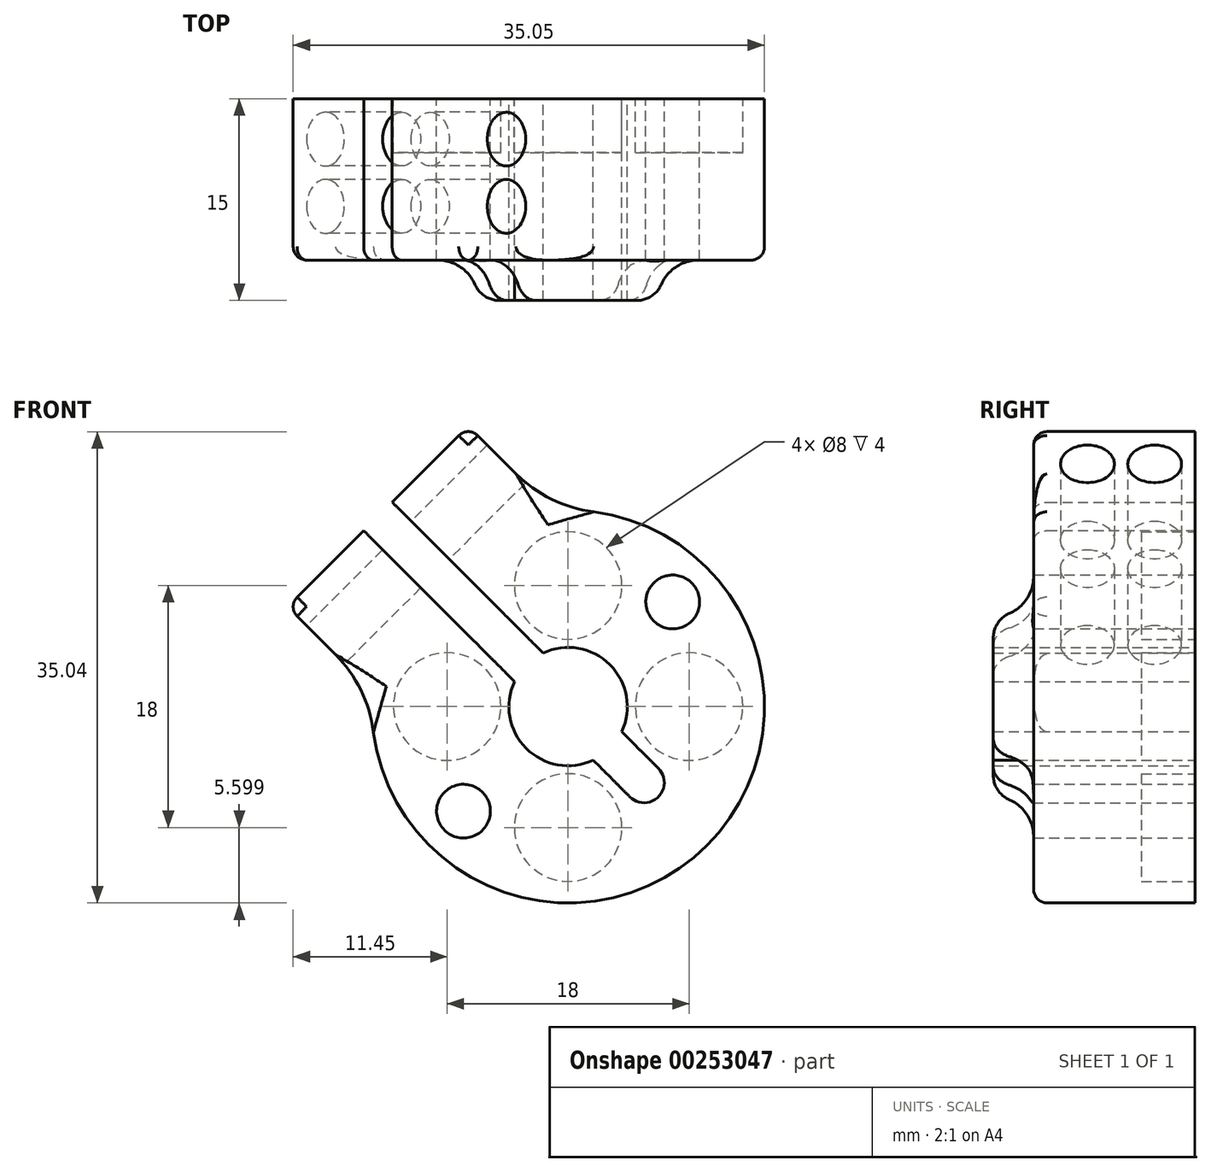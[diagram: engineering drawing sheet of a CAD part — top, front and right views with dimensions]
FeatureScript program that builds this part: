
annotation { "Feature Type Name" : "Feature", "Feature Type Description" : "" }
export const myFeature = defineFeature(function(context is Context, id is Id, definition is map)
    precondition{}
    {
        {
            var Q0;
            Q0=qCreatedBy(makeId("Right.planeOp"),FACE);
            var sketch = newSketch(context, id + "F0", { "sketchPlane" : qUnion([Q0])});
            skLineSegment(sketch, "E0", {"start": v(-60.78, -4.86) * mm, "end": v(-45.78, -4.86) * mm});
            skLineSegment(sketch, "E1", {"start": v(-45.78, -4.86) * mm, "end": v(-45.78, 5.34) * mm});
            skLineSegment(sketch, "E2", {"start": v(-45.78, 5.34) * mm, "end": v(-57.78, 5.34) * mm});
            skLineSegment(sketch, "E3", {"start": v(-57.78, 5.34) * mm, "end": v(-57.78, -2.16) * mm});
            skLineSegment(sketch, "E4", {"start": v(-57.78, -2.16) * mm, "end": v(-60.78, -2.16) * mm});
            skLineSegment(sketch, "E5", {"start": v(-60.78, -2.16) * mm, "end": v(-60.78, -4.86) * mm});
            skLineSegment(sketch, "E6", {"start": v(-43.04, -9.26) * mm, "end": v(-64.3, -9.26) * mm, "construction": true});
            skSolve(sketch);
        }
        {
            var Q0;
            Q0=qSketchRegion(id+"F0",true);
            var Q1;
            Q1=sQuery(id+"F0.wireOp",EDGE,"E6");
            revolve(context, id + "F1", {"entities" : qUnion([Q0]), "axis" : qUnion([Q1]), "revolveType" : RevolveType.FULL});
        }
        {
            var Q0;
            Q0=makeQuery(id+"F1.opRevolve","SWEPT_EDGE",EDGE,{"disambiguationData":[OSD([sQuery(id+"F0.wireOp",EDGE,"E4"),sQuery(id+"F0.wireOp",EDGE,"E5")])]});
            fillet(context, id + "F2", {"entities" : qUnion([Q0]), "radius" : 2 * mm, "tangentPropagation" : true, "allowEdgeOverflow" : false});
        }
        {
            var Q0;
            Q0=makeQuery(id+"F1.opRevolve","SWEPT_FACE",FACE,{"disambiguationData":[OSD([sQuery(id+"F0.wireOp",EDGE,"E1")])]});
            var sketch = newSketch(context, id + "F3", { "sketchPlane" : qUnion([Q0])});
            skCircle(sketch, "E7", {"center": v(0, -0.26) * mm, "radius": 4 * mm});
            skPoint(sketch, "E8", {"position": v(0, -9.26) * mm});
            skCircle(sketch, "E9.1.0", {"center": v(-9, -9.26) * mm, "radius": 4 * mm});
            skCircle(sketch, "E9.2.0", {"center": v(0, -18.26) * mm, "radius": 4 * mm});
            skCircle(sketch, "E9.3.0", {"center": v(9, -9.26) * mm, "radius": 4 * mm});
            skSolve(sketch);
        }
        {
            var Q0;
            Q0=makeQuery(id+"F3.imprint","IMPRINT",FACE,{"disambiguationData":[TD([[makeQuery(id+"F3.imprint","IMPRINT",EDGE,{"derivedFrom":sQuery(id+"F3.wireOp",EDGE,"E7")}),1.0]])]});
            var Q1;
            Q1=makeQuery(id+"F3.imprint","IMPRINT",FACE,{"disambiguationData":[TD([[makeQuery(id+"F3.imprint","IMPRINT",EDGE,{"derivedFrom":sQuery(id+"F3.wireOp",EDGE,"E9.1.0")}),1.0]])]});
            var Q2;
            Q2=makeQuery(id+"F3.imprint","IMPRINT",FACE,{"disambiguationData":[TD([[makeQuery(id+"F3.imprint","IMPRINT",EDGE,{"derivedFrom":sQuery(id+"F3.wireOp",EDGE,"E9.2.0")}),1.0]])]});
            var Q3;
            Q3=makeQuery(id+"F3.imprint","IMPRINT",FACE,{"disambiguationData":[TD([[makeQuery(id+"F3.imprint","IMPRINT",EDGE,{"derivedFrom":sQuery(id+"F3.wireOp",EDGE,"E9.3.0")}),1.0]])]});
            extrude(context, id + "F4", {"entities" : qUnion([Q0, Q1, Q2, Q3]), "operationType" : NewBodyOperationType.REMOVE, "oppositeDirection" : true, "depth" : 4 * mm});
        }
        {
            var Q0;
            Q0=makeQuery(id+"F1.opRevolve","SWEPT_FACE",FACE,{"disambiguationData":[OSD([sQuery(id+"F0.wireOp",EDGE,"E1")])]});
            var sketch = newSketch(context, id + "F5", { "sketchPlane" : qUnion([Q0])});
            skLineSegment(sketch, "E10.0", {"start": v(1.96, -9.42) * mm, "end": v(14.69, 3.3) * mm});
            skLineSegment(sketch, "E11.0", {"start": v(-0.16, -7.3) * mm, "end": v(12.57, 5.43) * mm});
            skLineSegment(sketch, "E12", {"start": v(12.57, 5.43) * mm, "end": v(14.69, 3.3) * mm});
            skLineSegment(sketch, "E13", {"start": v(-0.16, -7.3) * mm, "end": v(1.96, -9.42) * mm});
            skLineSegment(sketch, "E14", {"start": v(0, -9.26) * mm, "end": v(15.38, 6.12) * mm, "construction": true});
            skSolve(sketch);
        }
        {
            var Q0;
            Q0=qSketchRegion(id+"F5",true);
            extrude(context, id + "F6", {"entities" : qUnion([Q0]), "operationType" : NewBodyOperationType.REMOVE, "oppositeDirection" : true, "depth" : 25 * mm});
        }
        {
            var Q0;
            Q0=makeQuery(id+"F1.opRevolve","SWEPT_FACE",FACE,{"disambiguationData":[OSD([sQuery(id+"F0.wireOp",EDGE,"E1")])]});
            var sketch = newSketch(context, id + "F7", { "sketchPlane" : qUnion([Q0])});
            skPoint(sketch, "E15", {"position": v(0, -9.26) * mm});
            skLineSegment(sketch, "E16", {"start": v(7.14, 0) * mm, "end": v(13.08, 5.94) * mm});
            skPoint(sketch, "E16.startSnap0", {"position": v(7.66, -3.72) * mm});
            skLineSegment(sketch, "E17", {"start": v(13.08, 5.94) * mm, "end": v(7.42, 11.6) * mm});
            skLineSegment(sketch, "E18", {"start": v(7.42, 11.6) * mm, "end": v(1.12, 5.3) * mm});
            skLineSegment(sketch, "E19", {"start": v(1.12, 5.3) * mm, "end": v(7.14, 0) * mm});
            skLineSegment(sketch, "E20", {"start": v(0, -9.26) * mm, "end": v(12.98, 3.71) * mm, "construction": true});
            skLineSegment(sketch, "E21.MirrorCS", {"start": v(15.2, 3.82) * mm, "end": v(20.86, -1.84) * mm});
            skLineSegment(sketch, "E22.MirrorCS", {"start": v(20.86, -1.84) * mm, "end": v(14.56, -8.14) * mm});
            skLineSegment(sketch, "E23.MirrorCS", {"start": v(14.56, -8.14) * mm, "end": v(9.26, -2.12) * mm});
            skLineSegment(sketch, "E24.MirrorCS", {"start": v(9.26, -2.12) * mm, "end": v(15.2, 3.82) * mm});
            skSolve(sketch);
        }
        {
            var Q0;
            Q0=qSketchRegion(id+"F7",true);
            var Q1;
            Q1=makeQuery(id+"F1.opRevolve","SWEPT_FACE",FACE,{"disambiguationData":[OSD([sQuery(id+"F0.wireOp",EDGE,"E3")])]});
            extrude(context, id + "F8", {"entities" : qUnion([Q0]), "operationType" : NewBodyOperationType.ADD, "endBound" : BoundingType.UP_TO_SURFACE, "oppositeDirection" : true, "endBoundEntityFace" : qUnion([Q1]), "depth" : 25 * mm});
        }
        {
            var Q0;
            Q0=makeQuery(id+"F1.opRevolve","SWEPT_EDGE",EDGE,{"disambiguationData":[OSD([sQuery(id+"F0.wireOp",EDGE,"E3"),sQuery(id+"F0.wireOp",EDGE,"E4")])]});
            fillet(context, id + "F9", {"entities" : qUnion([Q0]), "radius" : 3 * mm, "tangentPropagation" : true, "allowEdgeOverflow" : false});
        }
        {
            var Q0;
            Q0=makeQuery(id+"F1.opRevolve","SWEPT_EDGE",EDGE,{"disambiguationData":[OSD([sQuery(id+"F0.wireOp",EDGE,"E2"),sQuery(id+"F0.wireOp",EDGE,"E3")])]});
            var Q1;
            Q1=makeQuery(id+"F8.opExtrude","CAP_EDGE",EDGE,{"disambiguationData":[OSD([sQuery(id+"F7.wireOp",EDGE,"E18")])],"isStart":false});
            var Q2;
            Q2=makeQuery(id+"F8.opExtrude","CAP_EDGE",EDGE,{"disambiguationData":[OSD([sQuery(id+"F7.wireOp",EDGE,"E17")])],"isStart":false});
            var Q3;
            Q3=makeQuery(id+"F8.opExtrude","CAP_EDGE",EDGE,{"disambiguationData":[OSD([sQuery(id+"F7.wireOp",EDGE,"E21.MirrorCS")])],"isStart":false});
            var Q4;
            Q4=makeQuery(id+"F8.opExtrude","CAP_EDGE",EDGE,{"disambiguationData":[OSD([sQuery(id+"F7.wireOp",EDGE,"E22.MirrorCS")])],"isStart":false});
            fillet(context, id + "F10", {"entities" : qUnion([Q0, Q1, Q2, Q3, Q4]), "radius" : 1 * mm, "tangentPropagation" : true, "allowEdgeOverflow" : false});
        }
        {
            var Q0;
            Q0=makeQuery(id+"F8.boolean.opBoolean","INTERSECT",EDGE,{"derivedFrom":[makeQuery(id+"F1.opRevolve","SWEPT_FACE",FACE,{"disambiguationData":[OSD([sQuery(id+"F0.wireOp",EDGE,"E2")])]}),makeQuery(id+"F8.opExtrude","SWEPT_FACE",FACE,{"disambiguationData":[OSD([sQuery(id+"F7.wireOp",EDGE,"E18")])]})]});
            var Q1;
            Q1=makeQuery(id+"F8.boolean.opBoolean","INTERSECT",EDGE,{"derivedFrom":[makeQuery(id+"F1.opRevolve","SWEPT_FACE",FACE,{"disambiguationData":[OSD([sQuery(id+"F0.wireOp",EDGE,"E2")])]}),makeQuery(id+"F8.opExtrude","SWEPT_FACE",FACE,{"disambiguationData":[OSD([sQuery(id+"F7.wireOp",EDGE,"E22.MirrorCS")])]})]});
            var Q2;
            Q2=makeQuery(id+"F10.opFillet","BLEND_EDGE",EDGE,{"blendedFrom":[makeQuery(id+"F8.opExtrude","CAP_EDGE",EDGE,{"disambiguationData":[OSD([sQuery(id+"F7.wireOp",EDGE,"E18")])],"isStart":false}),makeQuery(id+"F1.opRevolve","SWEPT_EDGE",EDGE,{"disambiguationData":[OSD([sQuery(id+"F0.wireOp",EDGE,"E2"),sQuery(id+"F0.wireOp",EDGE,"E3")])]})],"blendedInto":[]});
            var Q3;
            Q3=makeQuery(id+"F10.opFillet","BLEND_EDGE",EDGE,{"blendedFrom":[makeQuery(id+"F8.opExtrude","CAP_EDGE",EDGE,{"disambiguationData":[OSD([sQuery(id+"F7.wireOp",EDGE,"E22.MirrorCS")])],"isStart":false}),makeQuery(id+"F1.opRevolve","SWEPT_EDGE",EDGE,{"disambiguationData":[OSD([sQuery(id+"F0.wireOp",EDGE,"E2"),sQuery(id+"F0.wireOp",EDGE,"E3")])]})],"blendedInto":[]});
            fillet(context, id + "F11", {"entities" : qUnion([Q0, Q1, Q2, Q3]), "radius" : 10 * mm, "tangentPropagation" : true, "allowEdgeOverflow" : false});
        }
        {
            var Q0;
            Q0=makeQuery(id+"F10.opFillet","BLEND_EDGE",EDGE,{"blendedFrom":[makeQuery(id+"F8.opExtrude","CAP_EDGE",EDGE,{"disambiguationData":[OSD([sQuery(id+"F7.wireOp",EDGE,"E17")])],"isStart":false}),makeQuery(id+"F8.opExtrude","CAP_EDGE",EDGE,{"disambiguationData":[OSD([sQuery(id+"F7.wireOp",EDGE,"E18")])],"isStart":false})],"blendedInto":[]});
            var Q1;
            Q1=makeQuery(id+"F10.opFillet","BLEND_EDGE",EDGE,{"blendedFrom":[makeQuery(id+"F8.opExtrude","CAP_EDGE",EDGE,{"disambiguationData":[OSD([sQuery(id+"F7.wireOp",EDGE,"E21.MirrorCS")])],"isStart":false}),makeQuery(id+"F8.opExtrude","CAP_EDGE",EDGE,{"disambiguationData":[OSD([sQuery(id+"F7.wireOp",EDGE,"E22.MirrorCS")])],"isStart":false})],"blendedInto":[]});
            var Q2;
            Q2=makeQuery(id+"F8.opExtrude","SWEPT_EDGE",EDGE,{"disambiguationData":[OSD([sQuery(id+"F7.wireOp",EDGE,"E21.MirrorCS"),sQuery(id+"F7.wireOp",EDGE,"E22.MirrorCS")])]});
            var Q3;
            {var subQ0=sQuery(id+"F0.wireOp",EDGE,"E3");Q3=makeQuery(id+"F10.opFillet","BLEND_EDGE",EDGE,{"blendedFrom":[makeQuery(id+"F1.opRevolve","SWEPT_EDGE",EDGE,{"disambiguationData":[OSD([sQuery(id+"F0.wireOp",EDGE,"E2"),subQ0])]}),makeQuery(id+"F8.boolean.opBoolean","MERGE",FACE,{"derivedFrom":[makeQuery(id+"F1.opRevolve","SWEPT_FACE",FACE,{"disambiguationData":[OSD([subQ0])]}),makeQuery(id+"F8.opExtrude","CAP_FACE",FACE,{"disambiguationData":[OSD([sQuery(id+"F7.wireOp",EDGE,"E16"),sQuery(id+"F7.wireOp",EDGE,"E17"),sQuery(id+"F7.wireOp",EDGE,"E18"),sQuery(id+"F7.wireOp",EDGE,"E19")])],"isStart":false}),makeQuery(id+"F8.opExtrude","CAP_FACE",FACE,{"disambiguationData":[OSD([sQuery(id+"F7.wireOp",EDGE,"E21.MirrorCS"),sQuery(id+"F7.wireOp",EDGE,"E22.MirrorCS"),sQuery(id+"F7.wireOp",EDGE,"E23.MirrorCS"),sQuery(id+"F7.wireOp",EDGE,"E24.MirrorCS")])],"isStart":false})]})],"blendedInto":[makeQuery(id+"F8.boolean.opBoolean","MERGE",FACE,{"derivedFrom":[makeQuery(id+"F1.opRevolve","SWEPT_FACE",FACE,{"disambiguationData":[OSD([subQ0])]}),makeQuery(id+"F8.opExtrude","CAP_FACE",FACE,{"disambiguationData":[OSD([sQuery(id+"F7.wireOp",EDGE,"E16"),sQuery(id+"F7.wireOp",EDGE,"E17"),sQuery(id+"F7.wireOp",EDGE,"E18"),sQuery(id+"F7.wireOp",EDGE,"E19")])],"isStart":false}),makeQuery(id+"F8.opExtrude","CAP_FACE",FACE,{"disambiguationData":[OSD([sQuery(id+"F7.wireOp",EDGE,"E21.MirrorCS"),sQuery(id+"F7.wireOp",EDGE,"E22.MirrorCS"),sQuery(id+"F7.wireOp",EDGE,"E23.MirrorCS"),sQuery(id+"F7.wireOp",EDGE,"E24.MirrorCS")])],"isStart":false})]})]});}
            var Q4;
            {var subQ0=sQuery(id+"F7.wireOp",EDGE,"E18");Q4=makeQuery(id+"F10.opFillet","BLEND_EDGE",EDGE,{"blendedFrom":[makeQuery(id+"F8.opExtrude","CAP_EDGE",EDGE,{"disambiguationData":[OSD([subQ0])],"isStart":false}),makeQuery(id+"F8.boolean.opBoolean","MERGE",FACE,{"derivedFrom":[makeQuery(id+"F1.opRevolve","SWEPT_FACE",FACE,{"disambiguationData":[OSD([sQuery(id+"F0.wireOp",EDGE,"E3")])]}),makeQuery(id+"F8.opExtrude","CAP_FACE",FACE,{"disambiguationData":[OSD([sQuery(id+"F7.wireOp",EDGE,"E16"),sQuery(id+"F7.wireOp",EDGE,"E17"),subQ0,sQuery(id+"F7.wireOp",EDGE,"E19")])],"isStart":false}),makeQuery(id+"F8.opExtrude","CAP_FACE",FACE,{"disambiguationData":[OSD([sQuery(id+"F7.wireOp",EDGE,"E21.MirrorCS"),sQuery(id+"F7.wireOp",EDGE,"E22.MirrorCS"),sQuery(id+"F7.wireOp",EDGE,"E23.MirrorCS"),sQuery(id+"F7.wireOp",EDGE,"E24.MirrorCS")])],"isStart":false})]})],"blendedInto":[makeQuery(id+"F8.boolean.opBoolean","MERGE",FACE,{"derivedFrom":[makeQuery(id+"F1.opRevolve","SWEPT_FACE",FACE,{"disambiguationData":[OSD([sQuery(id+"F0.wireOp",EDGE,"E3")])]}),makeQuery(id+"F8.opExtrude","CAP_FACE",FACE,{"disambiguationData":[OSD([sQuery(id+"F7.wireOp",EDGE,"E16"),sQuery(id+"F7.wireOp",EDGE,"E17"),subQ0,sQuery(id+"F7.wireOp",EDGE,"E19")])],"isStart":false}),makeQuery(id+"F8.opExtrude","CAP_FACE",FACE,{"disambiguationData":[OSD([sQuery(id+"F7.wireOp",EDGE,"E21.MirrorCS"),sQuery(id+"F7.wireOp",EDGE,"E22.MirrorCS"),sQuery(id+"F7.wireOp",EDGE,"E23.MirrorCS"),sQuery(id+"F7.wireOp",EDGE,"E24.MirrorCS")])],"isStart":false})]})]});}
            var Q5;
            {var subQ0=sQuery(id+"F7.wireOp",EDGE,"E22.MirrorCS");Q5=makeQuery(id+"F10.opFillet","BLEND_EDGE",EDGE,{"blendedFrom":[makeQuery(id+"F8.opExtrude","CAP_EDGE",EDGE,{"disambiguationData":[OSD([subQ0])],"isStart":false}),makeQuery(id+"F8.boolean.opBoolean","MERGE",FACE,{"derivedFrom":[makeQuery(id+"F1.opRevolve","SWEPT_FACE",FACE,{"disambiguationData":[OSD([sQuery(id+"F0.wireOp",EDGE,"E3")])]}),makeQuery(id+"F8.opExtrude","CAP_FACE",FACE,{"disambiguationData":[OSD([sQuery(id+"F7.wireOp",EDGE,"E16"),sQuery(id+"F7.wireOp",EDGE,"E17"),sQuery(id+"F7.wireOp",EDGE,"E18"),sQuery(id+"F7.wireOp",EDGE,"E19")])],"isStart":false}),makeQuery(id+"F8.opExtrude","CAP_FACE",FACE,{"disambiguationData":[OSD([sQuery(id+"F7.wireOp",EDGE,"E21.MirrorCS"),subQ0,sQuery(id+"F7.wireOp",EDGE,"E23.MirrorCS"),sQuery(id+"F7.wireOp",EDGE,"E24.MirrorCS")])],"isStart":false})]})],"blendedInto":[makeQuery(id+"F8.boolean.opBoolean","MERGE",FACE,{"derivedFrom":[makeQuery(id+"F1.opRevolve","SWEPT_FACE",FACE,{"disambiguationData":[OSD([sQuery(id+"F0.wireOp",EDGE,"E3")])]}),makeQuery(id+"F8.opExtrude","CAP_FACE",FACE,{"disambiguationData":[OSD([sQuery(id+"F7.wireOp",EDGE,"E16"),sQuery(id+"F7.wireOp",EDGE,"E17"),sQuery(id+"F7.wireOp",EDGE,"E18"),sQuery(id+"F7.wireOp",EDGE,"E19")])],"isStart":false}),makeQuery(id+"F8.opExtrude","CAP_FACE",FACE,{"disambiguationData":[OSD([sQuery(id+"F7.wireOp",EDGE,"E21.MirrorCS"),subQ0,sQuery(id+"F7.wireOp",EDGE,"E23.MirrorCS"),sQuery(id+"F7.wireOp",EDGE,"E24.MirrorCS")])],"isStart":false})]})]});}
            fillet(context, id + "F12", {"entities" : qUnion([Q0, Q1, Q2, Q3, Q4, Q5]), "radius" : 1 * mm, "tangentPropagation" : true, "allowEdgeOverflow" : false});
        }
        {
            var Q0;
            Q0=makeQuery(id+"F8.opExtrude","SWEPT_FACE",FACE,{"disambiguationData":[OSD([sQuery(id+"F7.wireOp",EDGE,"E22.MirrorCS")])]});
            var sketch = newSketch(context, id + "F13", { "sketchPlane" : qUnion([Q0])});
            skCircle(sketch, "E25", {"center": v(48.78, 9.45) * mm, "radius": 2 * mm});
            skLineSegment(sketch, "E26", {"start": v(51.28, 3.88) * mm, "end": v(51.28, 12.45) * mm, "construction": true});
            skCircle(sketch, "E27.MirrorC", {"center": v(53.78, 9.45) * mm, "radius": 2 * mm});
            skSolve(sketch);
        }
        {
            var Q0;
            Q0=qSketchRegion(id+"F13",true);
            extrude(context, id + "F14", {"entities" : qUnion([Q0]), "operationType" : NewBodyOperationType.REMOVE, "endBound" : BoundingType.SYMMETRIC, "oppositeDirection" : true, "depth" : 50 * mm});
        }
        {
            var Q0;
            Q0=makeQuery(id+"F8.boolean.opBoolean","MERGE",FACE,{"derivedFrom":[makeQuery(id+"F1.opRevolve","SWEPT_FACE",FACE,{"disambiguationData":[OSD([sQuery(id+"F0.wireOp",EDGE,"E1")])]}),makeQuery(id+"F8.opExtrude","CAP_FACE",FACE,{"disambiguationData":[OSD([sQuery(id+"F7.wireOp",EDGE,"E16"),sQuery(id+"F7.wireOp",EDGE,"E17"),sQuery(id+"F7.wireOp",EDGE,"E18"),sQuery(id+"F7.wireOp",EDGE,"E19")])],"isStart":true}),makeQuery(id+"F8.opExtrude","CAP_FACE",FACE,{"disambiguationData":[OSD([sQuery(id+"F7.wireOp",EDGE,"E21.MirrorCS"),sQuery(id+"F7.wireOp",EDGE,"E22.MirrorCS"),sQuery(id+"F7.wireOp",EDGE,"E23.MirrorCS"),sQuery(id+"F7.wireOp",EDGE,"E24.MirrorCS")])],"isStart":true})]});
            var sketch = newSketch(context, id + "F15", { "sketchPlane" : qUnion([Q0])});
            skPoint(sketch, "E28", {"position": v(0, -9.26) * mm});
            skLineSegment(sketch, "E29", {"start": v(0, -9.26) * mm, "end": v(-5.66, -14.92) * mm, "construction": true});
            skLineSegment(sketch, "E30.0", {"start": v(1.06, -10.32) * mm, "end": v(-4.6, -15.98) * mm});
            skLineSegment(sketch, "E31.0", {"start": v(-1.06, -8.2) * mm, "end": v(-6.72, -13.86) * mm});
            skArc(sketch, "E32", {"start": v(-6.72, -13.86) * mm, "mid": v(-6.72, -15.98) * mm, "end": v(-4.6, -15.98) * mm});
            skLineSegment(sketch, "E33", {"start": v(-1.06, -8.2) * mm, "end": v(1.06, -10.32) * mm});
            skSolve(sketch);
        }
        {
            var Q0;
            Q0=qSketchRegion(id+"F15",true);
            extrude(context, id + "F16", {"entities" : qUnion([Q0]), "operationType" : NewBodyOperationType.REMOVE, "oppositeDirection" : true, "depth" : 25 * mm});
        }
        {
            var Q0;
            Q0=makeQuery(id+"F8.boolean.opBoolean","MERGE",FACE,{"derivedFrom":[makeQuery(id+"F1.opRevolve","SWEPT_FACE",FACE,{"disambiguationData":[OSD([sQuery(id+"F0.wireOp",EDGE,"E1")])]}),makeQuery(id+"F8.opExtrude","CAP_FACE",FACE,{"disambiguationData":[OSD([sQuery(id+"F7.wireOp",EDGE,"E16"),sQuery(id+"F7.wireOp",EDGE,"E17"),sQuery(id+"F7.wireOp",EDGE,"E18"),sQuery(id+"F7.wireOp",EDGE,"E19")])],"isStart":true}),makeQuery(id+"F8.opExtrude","CAP_FACE",FACE,{"disambiguationData":[OSD([sQuery(id+"F7.wireOp",EDGE,"E21.MirrorCS"),sQuery(id+"F7.wireOp",EDGE,"E22.MirrorCS"),sQuery(id+"F7.wireOp",EDGE,"E23.MirrorCS"),sQuery(id+"F7.wireOp",EDGE,"E24.MirrorCS")])],"isStart":true})]});
            var sketch = newSketch(context, id + "F17", { "sketchPlane" : qUnion([Q0])});
            skLineSegment(sketch, "E34", {"start": v(0, -9.26) * mm, "end": v(-7.78, -1.48) * mm, "construction": true});
            skCircle(sketch, "E35", {"center": v(-7.78, -1.48) * mm, "radius": 2 * mm});
            skLineSegment(sketch, "E36", {"start": v(0, -9.26) * mm, "end": v(15.24, 5.98) * mm, "construction": true});
            skCircle(sketch, "E37.MirrorC", {"center": v(7.78, -17.04) * mm, "radius": 2 * mm});
            skSolve(sketch);
        }
        {
            var Q0;
            Q0=qSketchRegion(id+"F17",true);
            extrude(context, id + "F18", {"entities" : qUnion([Q0]), "operationType" : NewBodyOperationType.REMOVE, "endBound" : BoundingType.SYMMETRIC, "oppositeDirection" : true, "depth" : 25 * mm});
        }
    });
